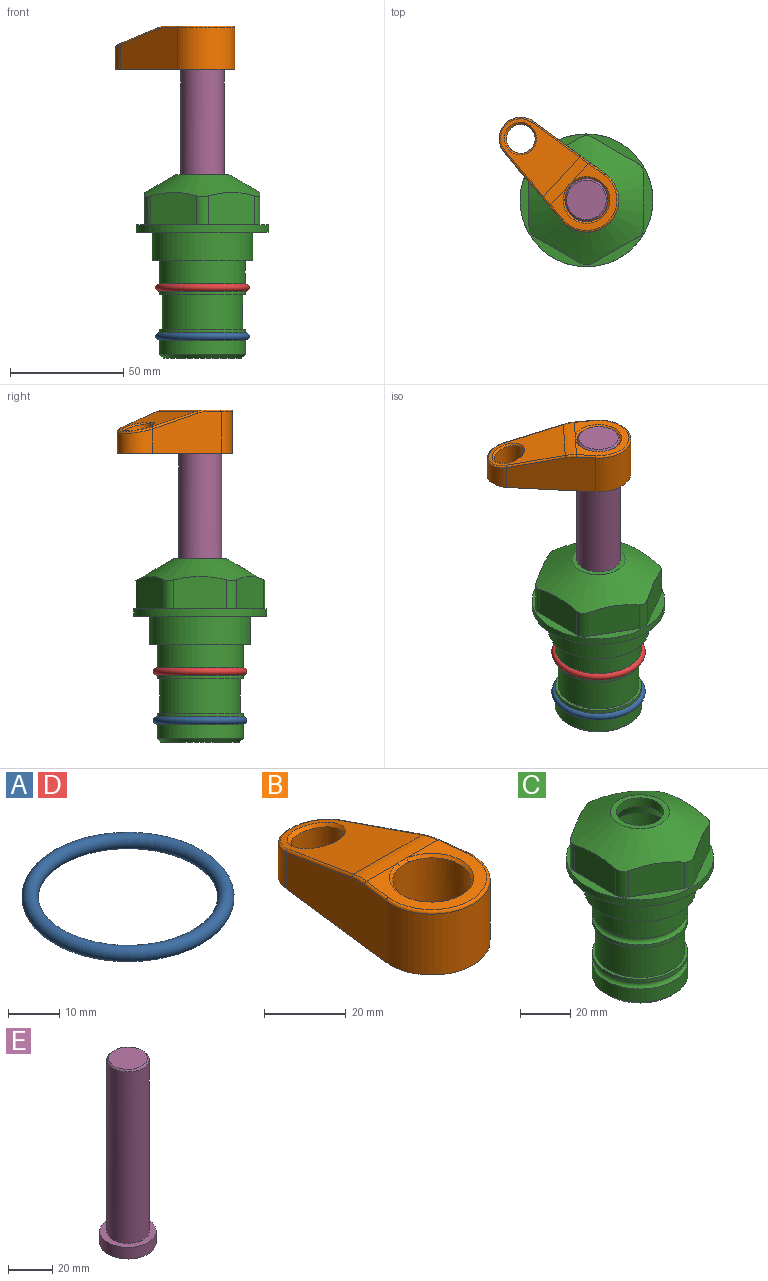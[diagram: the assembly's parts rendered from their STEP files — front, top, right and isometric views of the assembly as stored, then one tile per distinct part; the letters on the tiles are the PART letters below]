
ASSEMBLY  parts=5 mates=4
PART A: 1 faces, bbox 44.7x44.7x3.2 mm
  f0: torus R=19.05mm, axis (0,0,1), area 1193.9mm2
PART B: 31 faces, bbox 31.7x65.5x19.8 mm
  f0: plane 39.12x18.26mm, normal (0.99,0.12,0), area 612.2mm2, adj f1,f4,f7,f11,f13,f15
  f1: cylinder r=9.53mm len=18.91mm, axis (0,0,-1), area 296.1mm2, adj f0,f2,f7,f17
  f2: plane 39.12x18.26mm, normal (-0.99,0.12,0), area 612.2mm2, adj f1,f4,f7,f12,f14,f16
  f3: cylinder r=6.35mm len=12.7mm, axis (0,0,-1), area 362.4mm2, adj f7,f18
  f4: cylinder r=14.29mm len=28.58mm, axis (0,0,-1), area 882.2mm2, adj f0,f2,f7,f10
  f5: cylinder r=9.53mm len=19.05mm, axis (0,0,-1), area 1092.6mm2, adj f7,f19,f20
  f6: plane 26.99x23.69mm, normal (0,0,1), area 216.2mm2, adj f9,f10,f11,f12,f19
  f7: plane 63.5x28.58mm, normal (0,0,-1), area 661.8mm2, adj f0,f1,f2,f3,f4,f5,f22,f23
  f8: plane 33.52x23.6mm, normal (0,0.26,0.97), area 486mm2, adj f9,f15,f16,f17,f18
  f9: cylinder r=19.05mm len=24.72mm, axis (1,0,0), area 120.4mm2, adj f6,f8,f13,f14,f20
  f10: torus R=13.49mm, axis (0,0,1), area 59mm2, adj f4,f6,f11,f12
  f11: cylinder r=0.79mm len=8.67mm, axis (0.12,-0.99,0), area 10.8mm2, adj f0,f6,f10,f13
  f12: cylinder r=0.79mm len=8.67mm, axis (0.12,0.99,0), area 10.8mm2, adj f2,f6,f10,f14
  f13: bspline ~4.95x1.42mm, area 6.1mm2, adj f0,f9,f11,f15
  f14: bspline ~4.95x1.42mm, area 6.1mm2, adj f2,f9,f12,f16
  f15: cylinder r=0.79mm len=25.95mm, axis (0.12,-0.96,0.26), area 32.9mm2, adj f0,f8,f13,f17
  f16: cylinder r=0.79mm len=25.95mm, axis (0.12,0.96,-0.26), area 32.9mm2, adj f2,f8,f14,f17
  f17: bspline ~18.91x8.38mm, area 30mm2, adj f1,f8,f15,f16
  f18: bspline ~14.29x14.29mm, area 48.3mm2, adj f3,f8
  f19: cone r=9.53mm half-angle=45deg, axis (0,0,1), area 66.5mm2, adj f5,f6,f20
  f20: bspline ~3.22x0.96mm, area 3.5mm2, adj f5,f9,f19
  f21: plane 2.75x2.72mm, normal (0,0,-1), area 2.9mm2, adj f23,f25,f28
  f22: plane 23.05x15.88mm, normal (-0.99,-0.12,0), area 323.6mm2, adj f7,f25,f26,f27,f28,f29
  f23: plane 23.05x15.88mm, normal (0.99,-0.12,0), area 323.6mm2, adj f7,f21,f25,f27,f28,f30
  f24: cylinder r=9.53mm len=10.69mm, axis (0,0,-1), area 114.7mm2, adj f7,f27,f29,f30
  f25: cylinder r=12.7mm len=20.59mm, axis (0,0,-1), area 381.1mm2, adj f7,f21,f22,f23,f26,f28
  f26: plane 2.75x2.72mm, normal (0,0,-1), area 2.9mm2, adj f22,f25,f28
  f27: plane 19.72x18.37mm, normal (0,-0.26,-0.97), area 291.8mm2, adj f22,f23,f24,f28,f29,f30
  f28: cylinder r=15.88mm len=19.92mm, axis (1,0,0), area 54.8mm2, adj f21,f22,f23,f25,f26,f27
  f29: cylinder r=1.59mm len=11mm, axis (0,0,-1), area 34.7mm2, adj f7,f22,f24,f27
  f30: cylinder r=1.59mm len=11mm, axis (0,0,-1), area 34.7mm2, adj f7,f23,f24,f27
PART C: 36 faces, bbox 58.7x58.7x81 mm
  f0: cylinder r=17.78mm len=35.56mm, axis (0,0,1), area 1670.8mm2, adj f23,f24,f31
  f1: cylinder r=19.05mm len=38.1mm, axis (0,0,1), area 1191.9mm2, adj f26,f27,f30
  f2: plane 58.66x58.66mm, normal (0,0,-1), area 1150.6mm2, adj f3,f28
  f3: cylinder r=29.33mm len=58.66mm, axis (0,0,-1), area 585.1mm2, adj f2,f4
  f4: plane 58.66x58.66mm, normal (0,0,1), area 475.9mm2, adj f3,f5,f6,f7,f8,f9,f10,f11
  f5: plane 20.32x14.34mm, normal (-0.5,0.87,0), area 324.4mm2, adj f4,f15,f16,f17
  f6: plane 20.32x14.34mm, normal (0.5,0.87,0), area 324.4mm2, adj f4,f14,f15,f17
  f7: plane 23.48x14.34mm, normal (1,0,0), area 324.4mm2, adj f4,f13,f14,f17
  f8: plane 20.32x14.34mm, normal (0.5,-0.87,0), area 324.4mm2, adj f4,f12,f13,f17
  f9: plane 20.32x14.34mm, normal (-0.5,-0.87,0), area 324.4mm2, adj f4,f11,f12,f17
  f10: plane 23.48x14.34mm, normal (-1,0,0), area 324.4mm2, adj f4,f11,f16,f17
  f11: cylinder r=5.08mm len=12.85mm, axis (0,0,-1), area 67.2mm2, adj f4,f9,f10,f17
  f12: cylinder r=5.08mm len=12.85mm, axis (0,0,-1), area 67.2mm2, adj f4,f8,f9,f17
  f13: cylinder r=5.08mm len=12.85mm, axis (0,0,-1), area 67.2mm2, adj f4,f7,f8,f17
  f14: cylinder r=5.08mm len=12.85mm, axis (0,0,-1), area 67.2mm2, adj f4,f6,f7,f17
  f15: cylinder r=5.08mm len=12.85mm, axis (0,0,-1), area 67.2mm2, adj f4,f5,f6,f17
  f16: cylinder r=5.08mm len=12.85mm, axis (0,0,-1), area 67.2mm2, adj f4,f5,f10,f17
  f17: cone r=11.73mm half-angle=60deg, axis (0,0,-1), area 2071.8mm2, adj f5,f6,f7,f8,f9,f10,f11,f12
  f18: plane 23.46x23.46mm, normal (0,0,1), area 147.4mm2, adj f17,f35
  f19: plane 34.93x34.93mm, normal (0,0,-1), area 958mm2, adj f29
  f20: cylinder r=19.05mm len=38.1mm, axis (0,0,1), area 760.1mm2, adj f21,f29
  f21: torus R=19.05mm, axis (0,0,1), area 565.3mm2, adj f20,f22
  f22: cylinder r=19.05mm len=38.1mm, axis (0,0,1), area 190mm2, adj f21,f23
  f23: plane 38.1x38.1mm, normal (0,0,1), area 146.9mm2, adj f0,f22
  f24: plane 38.1x38.1mm, normal (0,0,-1), area 146.9mm2, adj f0,f25
  f25: cylinder r=19.05mm len=38.1mm, axis (0,0,1), area 190mm2, adj f24,f26
  f26: torus R=19.05mm, axis (0,0,1), area 565.3mm2, adj f1,f25
  f27: plane 44.45x44.45mm, normal (0,0,-1), area 411.7mm2, adj f1,f28
  f28: cylinder r=22.23mm len=44.45mm, axis (0,0,1), area 1773.5mm2, adj f2,f27
  f29: cone r=19.05mm half-angle=45deg, axis (0,0,1), area 257.5mm2, adj f19,f20
  f30: cylinder r=3.17mm len=6.75mm, axis (-1,0,0), area 128mm2, adj f1,f33
  f31: cylinder r=3.17mm len=6.35mm, axis (-1,0,0), area 102.5mm2, adj f0,f33
  f32: plane 25.4x25.4mm, normal (0,0,1), area 506.7mm2, adj f33
  f33: cylinder r=12.7mm len=66.42mm, axis (0,0,-1), area 5236.2mm2, adj f30,f31,f32,f34
  f34: cone r=9.53mm half-angle=30deg, axis (0,0,-1), area 443.4mm2, adj f33,f35
  f35: cylinder r=9.53mm len=19.05mm, axis (0,0,-1), area 240.9mm2, adj f18,f34
PART D: same geometry as A
PART E: 6 faces, bbox 25.4x25.4x101.6 mm
  f0: plane 17.46x17.46mm, normal (0,0,1), area 239.5mm2, adj f5
  f1: plane 25.4x25.4mm, normal (0,0,-1), area 506.7mm2, adj f2
  f2: cylinder r=12.7mm len=25.4mm, axis (0,0,1), area 506.7mm2, adj f1,f3
  f3: plane 25.4x25.4mm, normal (0,0,1), area 221.7mm2, adj f2,f4
  f4: cylinder r=9.53mm len=94.46mm, axis (0,0,1), area 5653mm2, adj f3,f5
  f5: cone r=8.73mm half-angle=45deg, axis (0,0,-1), area 64.4mm2, adj f0,f4
PLACE A t=(0,0,-21.59)mm
PLACE B rot(axis=(0,0,1),47.1deg) t=(0,0,27.55)mm
PLACE C at identity fixed
PLACE D at identity
PLACE E rot(axis=(0,0,1),47.1deg) t=(0,0,27.55)mm
MATE fastened D.f0 <-> C.f0  axis (0,0,1) through (0,0,-24.51)mm
MATE fastened E.f2 <-> B.f4  axis (0,0,1) through (0,0,91.05)mm
MATE cylindrical C.f0 <-> E.f2  axis (0,0,1) through (0,0,-50.55)mm
MATE fastened A.f0 <-> C.f0  axis (0,0,1) through (0,0,-46.1)mm
